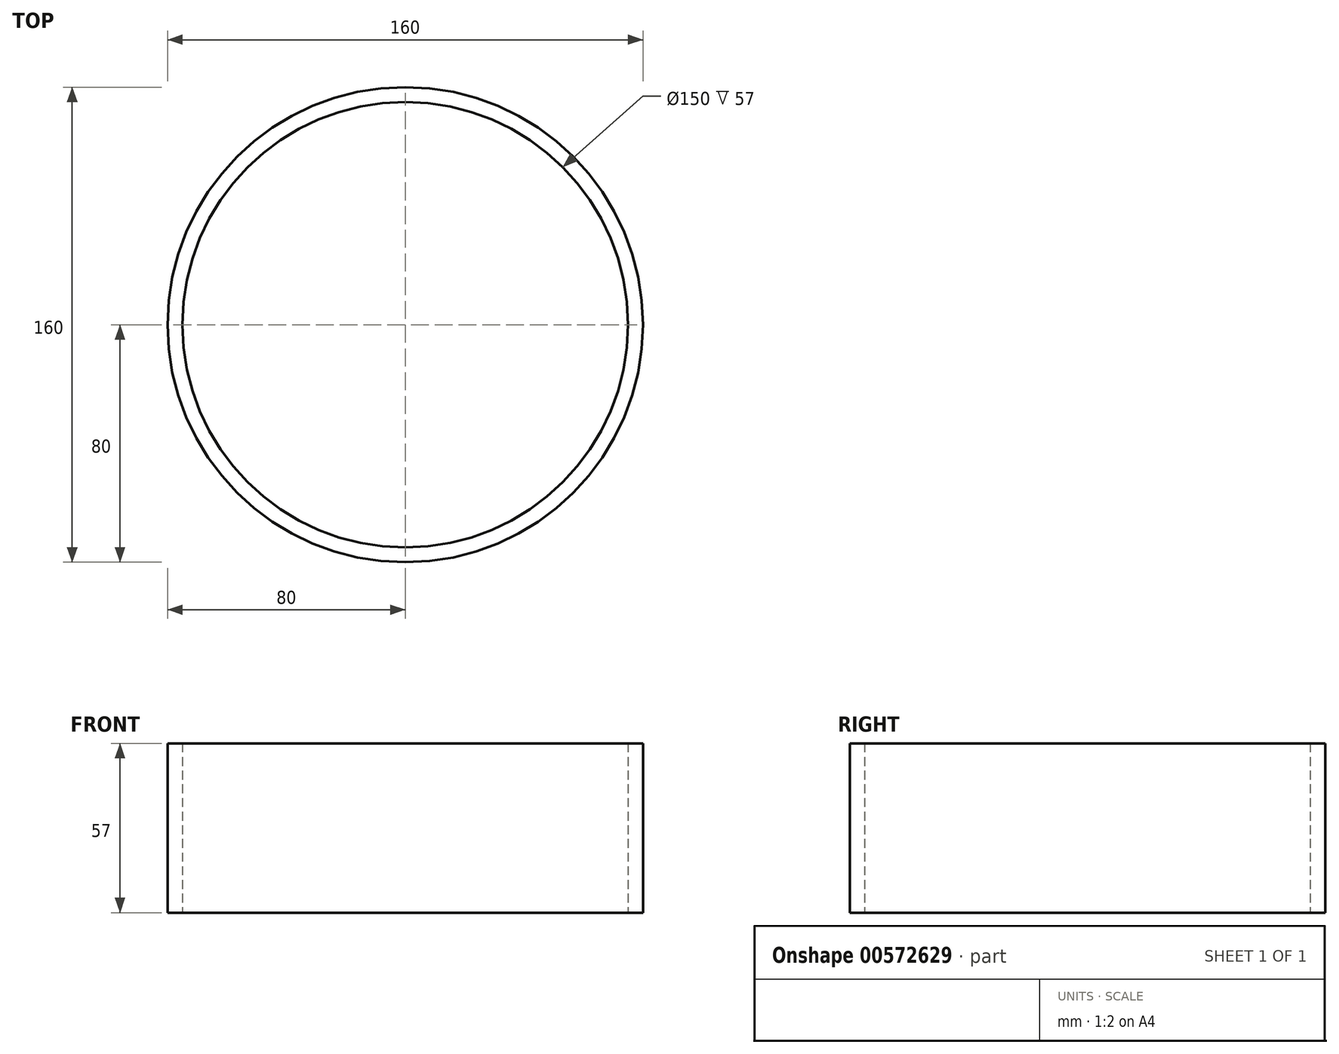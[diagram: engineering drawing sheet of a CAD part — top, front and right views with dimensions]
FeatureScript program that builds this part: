
annotation { "Feature Type Name" : "Feature", "Feature Type Description" : "" }
export const myFeature = defineFeature(function(context is Context, id is Id, definition is map)
    precondition{}
    {
        {
            var Q0;
            Q0=qCreatedBy(makeId("Top.planeOp"),FACE);
            var sketch = newSketch(context, id + "F0", { "sketchPlane" : qUnion([Q0])});
            skCircle(sketch, "E0", {"center": v(0, 0) * mm, "radius": 75 * mm});
            skCircle(sketch, "E1", {"center": v(0, 0) * mm, "radius": 80 * mm});
            skSolve(sketch);
        }
        {
            var Q0;
            Q0=makeQuery(id+"F0.imprint","IMPRINT",FACE,{"disambiguationData":[TD([[makeQuery(id+"F0.imprint","IMPRINT",EDGE,{"derivedFrom":sQuery(id+"F0.wireOp",EDGE,"E0")}),-1.0]])]});
            extrude(context, id + "F1", {"entities" : qUnion([Q0]), "depth" : 57 * mm, "offsetDistance" : 25.4 * mm});
        }
    });
